# Revit family: Faucet-Deck_Mount-Bath-KOHLER-COMPOSED-K-73078T
name_source: partatom
category: Plumbing Fixtures
revit_build: Autodesk Revit 2017 (Build: 20160225_1515(x64)
units: mm (PartAtom-declared; Revit-internal decimal feet)

## family parameters
Cut with Voids When Loaded = No
Host = Face
OmniClass Number = 23.31.11.00
OmniClass Title = Faucets
Part Type = Normal
Room Calculation Point = No
Round Connector Dimension = Use Diameter
Shared = No

## types (14) — shared parameters
ADA Compliant = No
Assembly Code = D2010
CW Connection = Yes
Cold Water Inlet = Cold Water Inlet
Date Modified = 07/01/2020
Default Elevation = 36"
Drain Included = No
Flow Rate = 3 GPM
HW Connection = Yes
Handle Clearance = 1 15/16"
Height = 6 1/2"
Hot Water Inlet = Hot Water Inlet
Length = 8 1/4"
Manufacturer = KOHLER Co.
Master Format 2014 = 22 41 39
Master Format 2014 Name = Residential Faucets, Supplies, and Trim
Material = Premium Metal Construction
Pressure = 80.00 psi
Product Name = COMPOSED
Spout Reach = 8 1/4"
URL = http://www.kohler.com.cn
Vent Connection = No
Waste Connection = No
Waste Water Outlet = Waste Water Outlet
WaterSense Certified = No

## per-type parameters (varying)
| type | Description | Finish | Handshower | Hanshower Height | Model | Product Documentation Link | Product Page URL | Type |
| CP-Polished Chrome | Modern classic 3 Hole bath filler with Handshower | Kohler-Metal-CP-Polished_Chrome | No | 9 5/8" | K-73038T-4-CP |  |  | 1 |
| TT-Titanium Silver | Modern classic 3 Hole bath filler with Handshower | Kohler-Metal-TT-Titanium_Silver | No | 9 5/8" | K-73038T-4-TT |  |  | 3 |
| AF-Flange Gold | Modern classic 3 Hole bath filler with Handshower | Kohler-Metal-AF-Flange_Gold | No | 9 5/8" | K-73038T-4-AF |  |  | 2 |
| 4E, CP-Polished Chrome | Modern classic 3 Hole bath filler with Handshower | Kohler-Metal-CP-Polished_Chrome | Yes | 10 7/16" | K-73038T-4E-CP |  |  | 4 |
| 4E, TT-Titanium Silver | Modern classic 3 Hole bath filler with Handshower | Kohler-Metal-TT-Titanium_Silver | Yes | 10 7/16" | K-73038T-4E-TT |  |  | 5 |
| B4, CP-Polished Chrome | 3 hole bathtub shower mixer | Kohler-Metal-CP-Polished_Chrome | Yes | 10 7/16" | K-73038T-B4-CP | https://files.kohler.com.cn | https://www.kohler.com.cn | 6 |
| B4, AF-Flange Gold | 3 hole bathtub shower mixer | Kohler-Metal-AF-Flange_Gold | Yes | 10 7/16" | K-73038T-B4-AF | https://files.kohler.com.cn | https://www.kohler.com.cn | 7 |
| B4, TT-Titanium Silver | 3 hole bathtub shower mixer | Kohler-Metal-TT-Titanium_Silver | Yes | 10 7/16" | K-73038T-B4-TT | https://files.kohler.com.cn | https://www.kohler.com.cn | 8 |
| B4, BN-Roman Silver | 3 hole bathtub shower mixer | Kohler-Metal-BN-Roman_Silver | Yes | 10 7/16" | K-73038T-B4-BN | https://files.kohler.com.cn | https://www.kohler.com.cn | 9 |
| B4, BV-Roman Copper | 3 hole bathtub shower mixer | Kohler-Metal-BV-Roman_Copper | Yes | 10 7/16" | K-73038T-B4-BV | https://files.kohler.com.cn | https://www.kohler.com.cn | 10 |
| B4, 2BL-Original Black | 3 hole bathtub shower mixer | Kohler-Metal-2BL-Original_Black | Yes | 10 7/16" | K-73038T-B4-2BL | https://files.kohler.com.cn | https://www.kohler.com.cn | 11 |
| B4, PGD-Eternal Gold | 3 hole bathtub shower mixer | Kohler-Metal-PGD-Eternal_Gold | Yes | 10 7/16" | K-73038T-B4-PGD | https://files.kohler.com.cn | https://www.kohler.com.cn | 12 |
| B4, RGD-Rose Gold | 3 hole bathtub shower mixer | Kohler-Metal-RGD-Rose_Gold | Yes | 10 7/16" | K-73038T-B4-RGD | https://files.kohler.com.cn | https://www.kohler.com.cn | 13 |
| B4, SN-Champagne Gold | 3 hole bathtub shower mixer | Kohler-Metal-SN-Champagne_Gold | Yes | 10 7/16" | K-73038T-B4-SN | https://files.kohler.com.cn | https://www.kohler.com.cn | 14 |

## geometry (parser evidence)
native form markers: Sweep x8
no freeform markers — native parametric forms only
